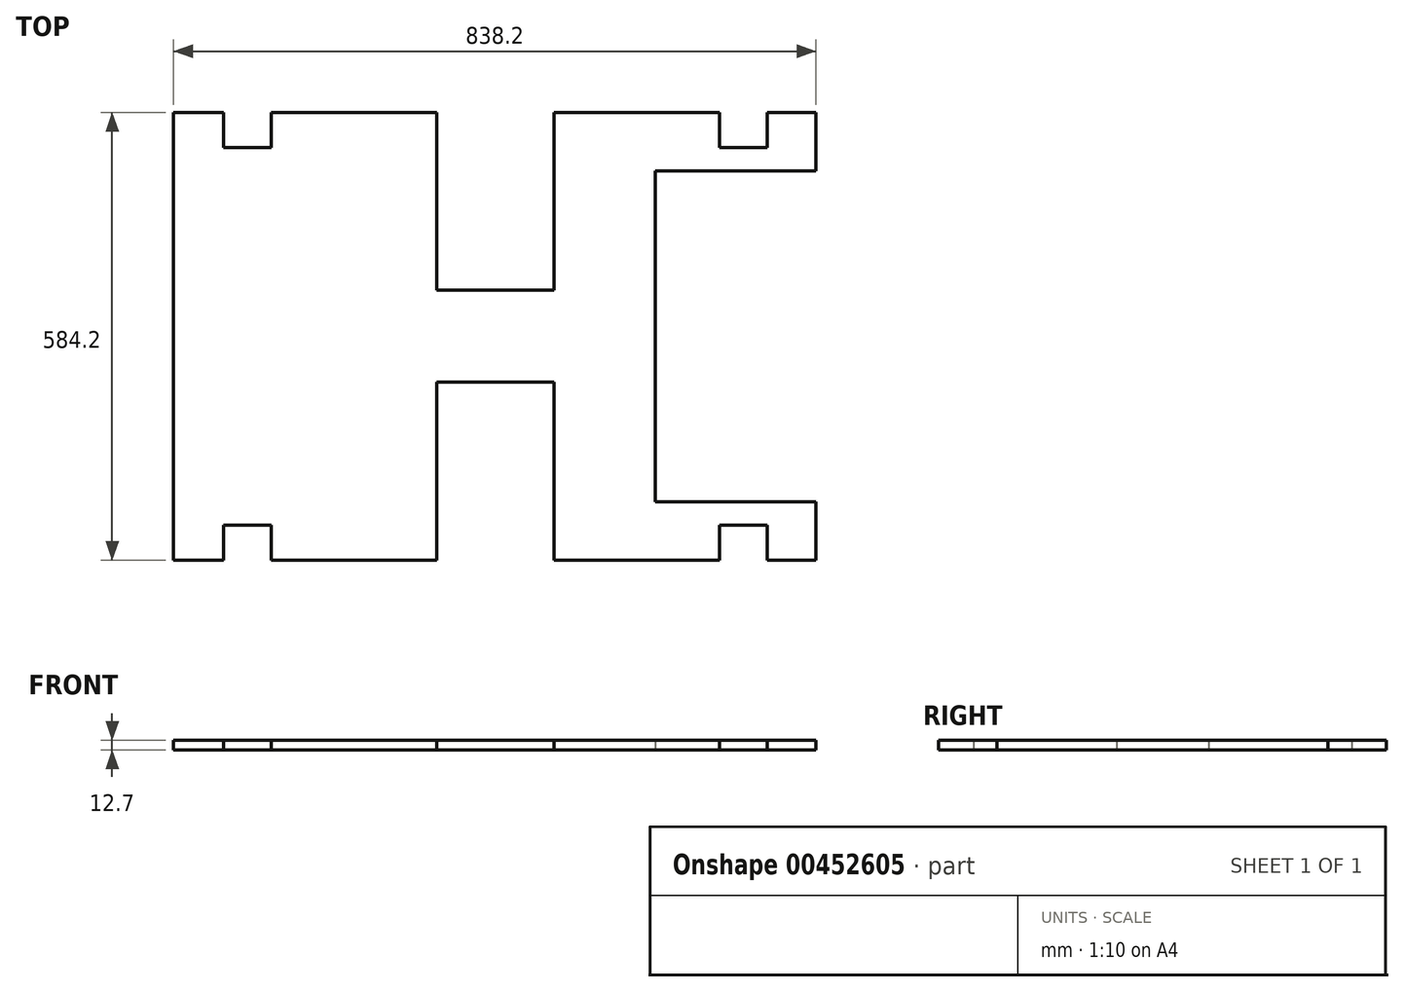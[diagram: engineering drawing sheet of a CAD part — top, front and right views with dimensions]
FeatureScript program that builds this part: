
annotation { "Feature Type Name" : "Feature", "Feature Type Description" : "" }
export const myFeature = defineFeature(function(context is Context, id is Id, definition is map)
    precondition{}
    {
        {
            var Q0;
            Q0=qCreatedBy(makeId("Top.planeOp"),FACE);
            var sketch = newSketch(context, id + "F0", { "sketchPlane" : qUnion([Q0])});
            skLineSegment(sketch, "E0.bottom", {"start": v(-419.9, 237.65) * mm, "end": v(418.3, 237.65) * mm});
            skLineSegment(sketch, "E0.top", {"start": v(-419.9, -346.55) * mm, "end": v(418.3, -346.55) * mm});
            skLineSegment(sketch, "E0.left", {"start": v(-419.9, 237.65) * mm, "end": v(-419.9, -346.55) * mm});
            skLineSegment(sketch, "E0.right", {"start": v(418.3, 237.65) * mm, "end": v(418.3, -346.55) * mm});
            skLineSegment(sketch, "E1.bottom", {"start": v(208.75, 161.45) * mm, "end": v(418.3, 161.45) * mm});
            skLineSegment(sketch, "E1.top", {"start": v(208.75, -270.35) * mm, "end": v(418.3, -270.35) * mm});
            skLineSegment(sketch, "E1.left", {"start": v(208.75, 161.45) * mm, "end": v(208.75, -270.35) * mm});
            skLineSegment(sketch, "E1.right", {"start": v(418.3, 161.45) * mm, "end": v(418.3, -270.35) * mm});
            skLineSegment(sketch, "E2.bottom", {"start": v(76.33, -114.42) * mm, "end": v(-76.33, -114.42) * mm});
            skLineSegment(sketch, "E2.top", {"start": v(76.33, -385.18) * mm, "end": v(-76.33, -385.18) * mm});
            skLineSegment(sketch, "E2.left", {"start": v(76.33, -114.42) * mm, "end": v(76.33, -385.18) * mm});
            skLineSegment(sketch, "E2.right", {"start": v(-76.33, -114.42) * mm, "end": v(-76.33, -385.18) * mm});
            skPoint(sketch, "E2.middle", {"position": v(0, -249.8) * mm});
            skLineSegment(sketch, "E3", {"start": v(208.75, -54.45) * mm, "end": v(-168.51, -54.45) * mm, "construction": true});
            skLineSegment(sketch, "E4.MirrorCS", {"start": v(76.33, 5.52) * mm, "end": v(76.33, 276.28) * mm});
            skLineSegment(sketch, "E5.MirrorCS", {"start": v(76.33, 5.52) * mm, "end": v(-76.33, 5.52) * mm});
            skLineSegment(sketch, "E6.MirrorCS", {"start": v(-76.33, 5.52) * mm, "end": v(-76.33, 276.28) * mm});
            skLineSegment(sketch, "E7.MirrorCS", {"start": v(76.33, 276.28) * mm, "end": v(-76.33, 276.28) * mm});
            skLineSegment(sketch, "E8.bottom", {"start": v(292.67, 192.16) * mm, "end": v(354.44, 192.16) * mm});
            skLineSegment(sketch, "E8.top", {"start": v(292.67, 274.66) * mm, "end": v(354.44, 274.66) * mm});
            skLineSegment(sketch, "E8.left", {"start": v(292.67, 192.16) * mm, "end": v(292.67, 274.66) * mm});
            skLineSegment(sketch, "E8.right", {"start": v(354.44, 192.16) * mm, "end": v(354.44, 274.66) * mm});
            skPoint(sketch, "E8.middle", {"position": v(323.56, 233.4) * mm});
            skLineSegment(sketch, "E9.MirrorCS", {"start": v(292.67, -301.06) * mm, "end": v(354.44, -301.06) * mm});
            skLineSegment(sketch, "E10.MirrorCS", {"start": v(292.67, -301.06) * mm, "end": v(292.67, -383.56) * mm});
            skLineSegment(sketch, "E11.MirrorCS", {"start": v(354.44, -301.06) * mm, "end": v(354.44, -383.56) * mm});
            skLineSegment(sketch, "E12.MirrorCS", {"start": v(292.67, -383.56) * mm, "end": v(354.44, -383.56) * mm});
            skLineSegment(sketch, "E13", {"start": v(0, -249.8) * mm, "end": v(0, 491.19) * mm, "construction": true});
            skLineSegment(sketch, "E14.MirrorCS", {"start": v(-354.44, 192.16) * mm, "end": v(-354.44, 274.66) * mm});
            skLineSegment(sketch, "E15.MirrorCS", {"start": v(419.9, 237.65) * mm, "end": v(-418.3, 237.65) * mm});
            skLineSegment(sketch, "E16.MirrorCS", {"start": v(-292.67, 192.16) * mm, "end": v(-292.67, 274.66) * mm});
            skLineSegment(sketch, "E17.MirrorCS", {"start": v(-292.67, 274.66) * mm, "end": v(-354.44, 274.66) * mm});
            skPoint(sketch, "E18.MirrorP", {"position": v(-323.56, 233.4) * mm});
            skLineSegment(sketch, "E19.MirrorCS", {"start": v(-292.67, 192.16) * mm, "end": v(-354.44, 192.16) * mm});
            skLineSegment(sketch, "E20.MirrorCS", {"start": v(-354.44, -301.06) * mm, "end": v(-354.44, -383.56) * mm});
            skLineSegment(sketch, "E21.MirrorCS", {"start": v(-292.67, -383.56) * mm, "end": v(-354.44, -383.56) * mm});
            skLineSegment(sketch, "E22.MirrorCS", {"start": v(-292.67, -301.06) * mm, "end": v(-354.44, -301.06) * mm});
            skLineSegment(sketch, "E23.MirrorCS", {"start": v(-292.67, -301.06) * mm, "end": v(-292.67, -383.56) * mm});
            skSolve(sketch);
        }
        {
            var Q0;
            Q0=makeQuery(id+"F0.imprint","IMPRINT",FACE,{"disambiguationData":[TD([[makeQuery(id+"F0.imprint","IMPRINT",EDGE,{"derivedFrom":sQuery(id+"F0.wireOp",EDGE,"E0.bottom")}),-1.0]])]});
            extrude(context, id + "F1", {"entities" : qUnion([Q0]), "depth" : 12.7 * mm});
        }
    });
